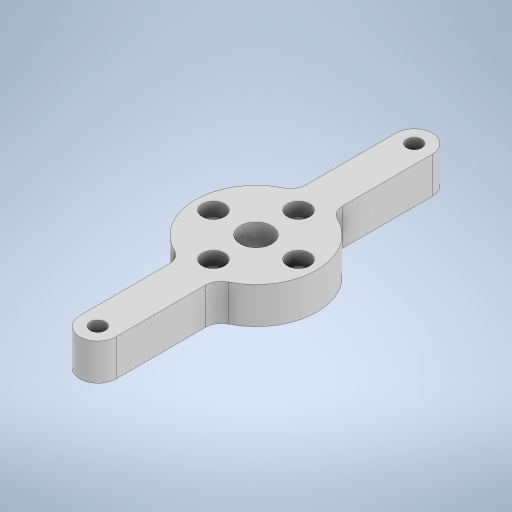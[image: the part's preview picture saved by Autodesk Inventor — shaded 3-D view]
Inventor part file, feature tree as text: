
AUTODESK INVENTOR PART (.ipt)
format: ipt  version: 2024.2 (Build 282272000, 272)  size: 306,688 bytes
history: native  units: mm
features: sketch x5, extrude x3, hole x2, projected_geometry x2, other x1
ambient origin geometry x8: Origin, YZ Plane, XZ Plane, XY Plane, X Axis, Y Axis, Z Axis, Center Point
bodies: Body1 (feature_tree)
feature tree (13):
  other  "솔리드1"
  extrude  "돌출1"  Depth=6.0mm TaperAngle=0.0deg
  hole  "구멍1"  [1 undecoded]
  extrude  "돌출2"  Depth=10.0mm
  hole  "구멍2"  [1 undecoded]
  extrude  "Extrusion3"  Depth=10.0mm
  sketch  "스케치1"
  sketch  "스케치2"
  sketch  "스케치3"
  projected_geometry  "투영된 루프1"
  sketch  "스케치4"
  projected_geometry  "투영된 루프2"
  sketch  "Sketch5"  dims[d0=20.0mm d1=6.0mm d2=0.0mm d3=14.0mm d4=2.1mm d5=4.0mm d6=3.7mm d7=2.2mm d8=90.0deg d9=4.0mm d10=0.0mm d11=4.0mm d12=4.0mm d13=26.0mm d14=26.0mm d15=3.0mm d19=5.0mm d20=3.0mm d21=6.0mm d22=0.0mm d23=2.5mm d24=3.0mm d25=4.0mm d26=2.2mm d27=90.0deg d28=3.0mm d29=0.0mm d30=5.2mm d31=10.0mm d32=0.0mm]
note: 2 required parameter values undecoded (feature->parameter linkage not recoverable at this tier; creation-order binding heuristic only, values carry confidence <= 0.55)
